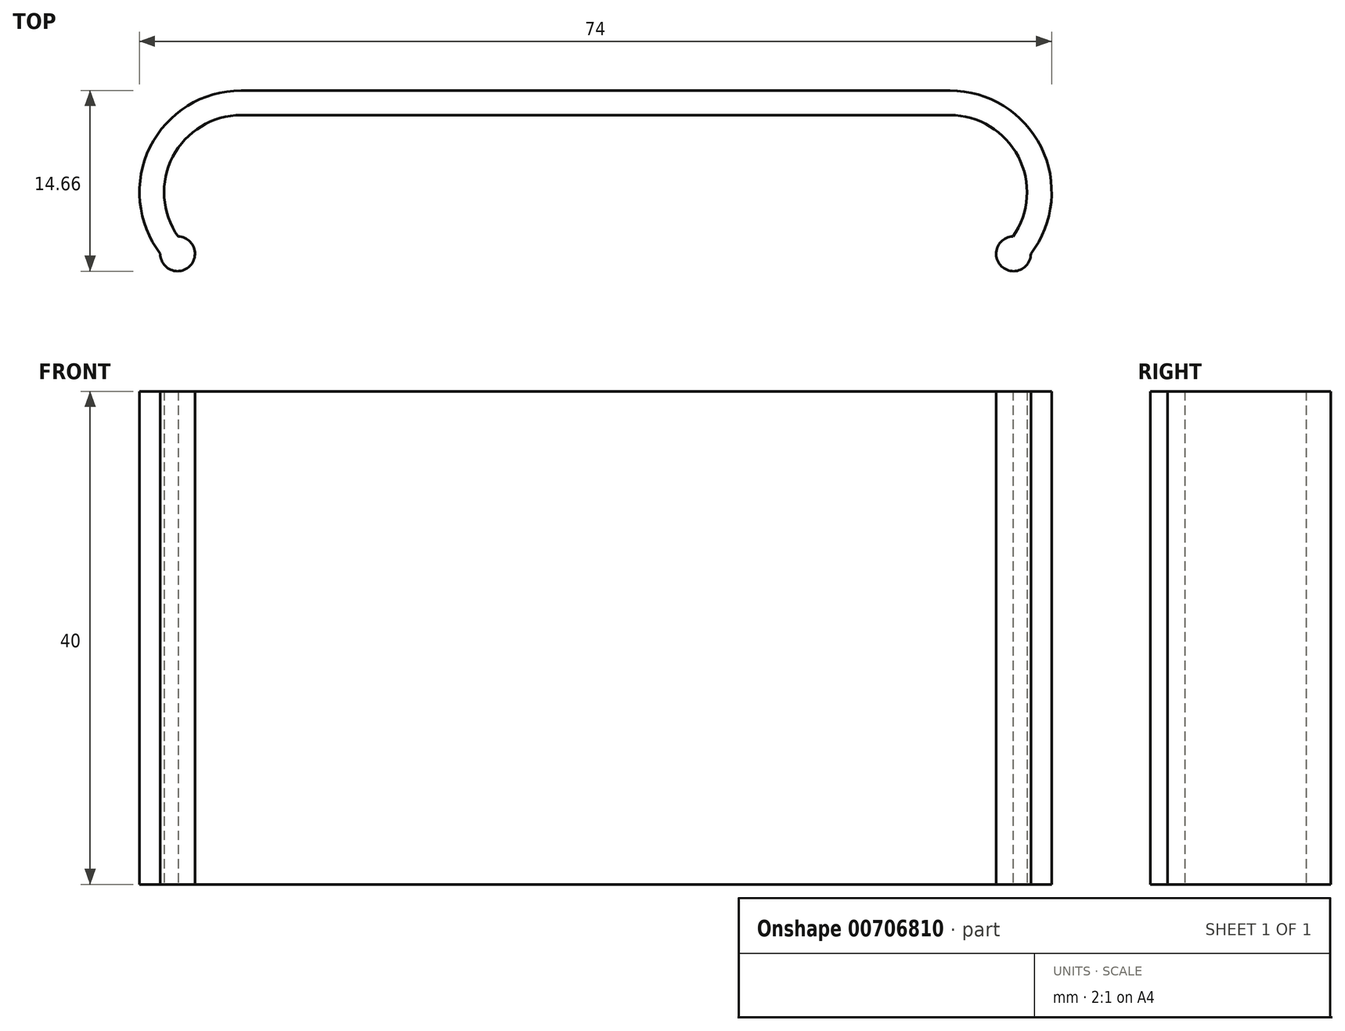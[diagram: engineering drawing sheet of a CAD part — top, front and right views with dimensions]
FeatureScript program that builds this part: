
annotation { "Feature Type Name" : "Feature", "Feature Type Description" : "" }
export const myFeature = defineFeature(function(context is Context, id is Id, definition is map)
    precondition{}
    {
        {
            var Q0;
            Q0=qCreatedBy(makeId("Top.planeOp"),FACE);
            var sketch = newSketch(context, id + "F0", { "sketchPlane" : qUnion([Q0])});
            skLineSegment(sketch, "E0.bottom", {"start": v(-28.75, 6.25) * mm, "end": v(28.75, 6.25) * mm});
            skLineSegment(sketch, "E0.top", {"start": v(-28.75, -6.25) * mm, "end": v(28.75, -6.25) * mm});
            skLineSegment(sketch, "E0.left", {"start": v(-28.75, 6.25) * mm, "end": v(-28.75, -6.25) * mm});
            skLineSegment(sketch, "E0.right", {"start": v(28.75, 6.25) * mm, "end": v(28.75, -6.25) * mm});
            skLineSegment(sketch, "E1.bottom", {"start": v(-28.75, 8.25) * mm, "end": v(28.75, 8.25) * mm});
            skLineSegment(sketch, "E1.top", {"start": v(-28.75, -8.25) * mm, "end": v(28.75, -8.25) * mm});
            skLineSegment(sketch, "E1.left", {"start": v(-28.75, 8.25) * mm, "end": v(-28.75, -8.25) * mm});
            skLineSegment(sketch, "E1.right", {"start": v(28.75, 8.25) * mm, "end": v(28.75, -8.25) * mm});
            skCircle(sketch, "E2", {"center": v(28.75, 0) * mm, "radius": 6.25 * mm});
            skCircle(sketch, "E3", {"center": v(28.75, 0) * mm, "radius": 8.25 * mm});
            skCircle(sketch, "E4", {"center": v(-28.75, 0) * mm, "radius": 6.25 * mm});
            skCircle(sketch, "E5", {"center": v(-28.75, 0) * mm, "radius": 8.25 * mm});
            skLineSegment(sketch, "E6", {"start": v(-47.39, -5) * mm, "end": v(64.54, -5) * mm});
            skPoint(sketch, "E7", {"position": v(-33.9, -5) * mm});
            skPoint(sketch, "E8", {"position": v(-35.31, -5) * mm});
            skPoint(sketch, "E9", {"position": v(-32.5, -5) * mm});
            skPoint(sketch, "E10", {"position": v(32.5, -5) * mm});
            skPoint(sketch, "E11", {"position": v(35.31, -5) * mm});
            skPoint(sketch, "E12", {"position": v(33.9, -5) * mm});
            skCircle(sketch, "E13", {"center": v(33.9, -5) * mm, "radius": 1.4 * mm});
            skCircle(sketch, "E14", {"center": v(-33.9, -5) * mm, "radius": 1.4 * mm});
            skPoint(sketch, "E15", {"position": v(-35, 0) * mm});
            skPoint(sketch, "E16", {"position": v(35, 0) * mm});
            skSolve(sketch);
        }
        {
            var Q0;
            {var subQ5=sQuery(id+"F0.wireOp",EDGE,"E1.bottom");Q0=makeQuery(id+"F0.imprint","IMPRINT",FACE,{"disambiguationData":[TD([[makeQuery(id+"F0.imprint","IMPRINT",EDGE,{"derivedFrom":subQ5}),-1.0]])]});}
            var Q1;
            {var subQ1=sQuery(id+"F0.wireOp",EDGE,"E0.bottom");var subQ3=sQuery(id+"F0.wireOp",EDGE,"E5");var subQ4=makeQuery(id+"F0.imprint","INTERSECT",VERTEX,{"derivedFrom":[subQ1,subQ3]});Q1=makeQuery(id+"F0.imprint","IMPRINT",FACE,{"disambiguationData":[TD([[makeQuery(id+"F0.imprint","IMPRINT",EDGE,{"disambiguationData":[TD([[subQ4,1.0]])],"derivedFrom":subQ1}),1.0]])]});}
            var Q2;
            {var subQ1=sQuery(id+"F0.wireOp",EDGE,"E0.bottom");var subQ3=sQuery(id+"F0.wireOp",EDGE,"E3");var subQ4=makeQuery(id+"F0.imprint","INTERSECT",VERTEX,{"derivedFrom":[subQ1,subQ3]});Q2=makeQuery(id+"F0.imprint","IMPRINT",FACE,{"disambiguationData":[TD([[makeQuery(id+"F0.imprint","IMPRINT",EDGE,{"disambiguationData":[TD([[subQ4,-1.0]])],"derivedFrom":subQ1}),1.0]])]});}
            var Q3;
            {var subQ0=sQuery(id+"F0.wireOp",EDGE,"E4");var subQ5=sQuery(id+"F0.wireOp",EDGE,"E14");var subQ6=makeQuery(id+"F0.imprint","INTERSECT",VERTEX,{"derivedFrom":[subQ0,subQ5]});Q3=makeQuery(id+"F0.imprint","IMPRINT",FACE,{"disambiguationData":[TD([[makeQuery(id+"F0.imprint","IMPRINT",EDGE,{"disambiguationData":[TD([[subQ6,1.0]])],"derivedFrom":subQ0}),-1.0]])]});}
            var Q4;
            {var subQ0=sQuery(id+"F0.wireOp",EDGE,"E14");var subQ1=sQuery(id+"F0.wireOp",EDGE,"E4");var subQ2=makeQuery(id+"F0.imprint","INTERSECT",VERTEX,{"derivedFrom":[subQ1,subQ0]});Q4=makeQuery(id+"F0.imprint","IMPRINT",FACE,{"disambiguationData":[TD([[makeQuery(id+"F0.imprint","IMPRINT",EDGE,{"disambiguationData":[TD([[subQ2,-1.0]])],"derivedFrom":subQ1}),-1.0]])]});}
            var Q5;
            {var subQ0=sQuery(id+"F0.wireOp",EDGE,"E14");var subQ1=sQuery(id+"F0.wireOp",EDGE,"E5");var subQ2=makeQuery(id+"F0.imprint","INTERSECT",VERTEX,{"derivedFrom":[subQ1,subQ0]});Q5=makeQuery(id+"F0.imprint","IMPRINT",FACE,{"disambiguationData":[TD([[makeQuery(id+"F0.imprint","IMPRINT",EDGE,{"disambiguationData":[TD([[subQ2,1.0]])],"derivedFrom":subQ1}),-1.0]])]});}
            var Q6;
            {var subQ0=sQuery(id+"F0.wireOp",EDGE,"E14");var subQ1=sQuery(id+"F0.wireOp",EDGE,"E5");var subQ2=makeQuery(id+"F0.imprint","INTERSECT",VERTEX,{"derivedFrom":[subQ1,subQ0]});Q6=makeQuery(id+"F0.imprint","IMPRINT",FACE,{"disambiguationData":[TD([[makeQuery(id+"F0.imprint","IMPRINT",EDGE,{"disambiguationData":[TD([[subQ2,1.0]])],"derivedFrom":subQ1}),1.0]])]});}
            var Q7;
            {var subQ0=sQuery(id+"F0.wireOp",EDGE,"E14");var subQ1=sQuery(id+"F0.wireOp",EDGE,"E4");var subQ2=makeQuery(id+"F0.imprint","INTERSECT",VERTEX,{"derivedFrom":[subQ1,subQ0]});Q7=makeQuery(id+"F0.imprint","IMPRINT",FACE,{"disambiguationData":[TD([[makeQuery(id+"F0.imprint","IMPRINT",EDGE,{"disambiguationData":[TD([[subQ2,-1.0]])],"derivedFrom":subQ1}),1.0]])]});}
            var Q8;
            {var subQ0=sQuery(id+"F0.wireOp",EDGE,"E2");var subQ5=sQuery(id+"F0.wireOp",EDGE,"E13");var subQ7=makeQuery(id+"F0.imprint","INTERSECT",VERTEX,{"derivedFrom":[subQ0,subQ5]});Q8=makeQuery(id+"F0.imprint","IMPRINT",FACE,{"disambiguationData":[TD([[makeQuery(id+"F0.imprint","IMPRINT",EDGE,{"disambiguationData":[TD([[subQ7,-1.0]])],"derivedFrom":subQ0}),-1.0]])]});}
            var Q9;
            {var subQ0=sQuery(id+"F0.wireOp",EDGE,"E13");var subQ1=sQuery(id+"F0.wireOp",EDGE,"E3");var subQ2=makeQuery(id+"F0.imprint","INTERSECT",VERTEX,{"derivedFrom":[subQ1,subQ0]});Q9=makeQuery(id+"F0.imprint","IMPRINT",FACE,{"disambiguationData":[TD([[makeQuery(id+"F0.imprint","IMPRINT",EDGE,{"disambiguationData":[TD([[subQ2,-1.0]])],"derivedFrom":subQ1}),1.0]])]});}
            var Q10;
            {var subQ0=sQuery(id+"F0.wireOp",EDGE,"E13");var subQ1=sQuery(id+"F0.wireOp",EDGE,"E2");var subQ2=makeQuery(id+"F0.imprint","INTERSECT",VERTEX,{"derivedFrom":[subQ1,subQ0]});Q10=makeQuery(id+"F0.imprint","IMPRINT",FACE,{"disambiguationData":[TD([[makeQuery(id+"F0.imprint","IMPRINT",EDGE,{"disambiguationData":[TD([[subQ2,1.0]])],"derivedFrom":subQ1}),-1.0]])]});}
            var Q11;
            {var subQ0=sQuery(id+"F0.wireOp",EDGE,"E13");var subQ1=sQuery(id+"F0.wireOp",EDGE,"E2");var subQ2=makeQuery(id+"F0.imprint","INTERSECT",VERTEX,{"derivedFrom":[subQ1,subQ0]});Q11=makeQuery(id+"F0.imprint","IMPRINT",FACE,{"disambiguationData":[TD([[makeQuery(id+"F0.imprint","IMPRINT",EDGE,{"disambiguationData":[TD([[subQ2,1.0]])],"derivedFrom":subQ1}),1.0]])]});}
            var Q12;
            {var subQ0=sQuery(id+"F0.wireOp",EDGE,"E13");var subQ1=sQuery(id+"F0.wireOp",EDGE,"E3");var subQ2=makeQuery(id+"F0.imprint","INTERSECT",VERTEX,{"derivedFrom":[subQ1,subQ0]});Q12=makeQuery(id+"F0.imprint","IMPRINT",FACE,{"disambiguationData":[TD([[makeQuery(id+"F0.imprint","IMPRINT",EDGE,{"disambiguationData":[TD([[subQ2,-1.0]])],"derivedFrom":subQ1}),-1.0]])]});}
            extrude(context, id + "F1", {"entities" : qUnion([Q0, Q1, Q2, Q3, Q4, Q5, Q6, Q7, Q8, Q9, Q10, Q11, Q12]), "endBound" : BoundingType.SYMMETRIC, "depth" : 40 * mm, "offsetDistance" : 25 * mm});
        }
    });
